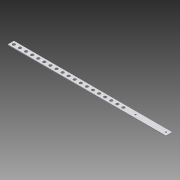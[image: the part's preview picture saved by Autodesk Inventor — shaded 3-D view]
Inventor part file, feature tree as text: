
AUTODESK INVENTOR PART (.ipt)
format: ipt  version: 2015 (Build 190159000, 159)  size: 151,040 bytes
history: native  units: in
note: dims shown in document units (in); Inventor stores cm internally (conversion verified against a paired STEP export)
features: sketch x5, projected_geometry x4, extrude x3, hole x2, pattern_linear x1
ambient origin geometry x8: Origin, YZ Plane, XZ Plane, XY Plane, X Axis, Y Axis, Z Axis, Center Point
bodies: Solid1 (feature_tree)
feature tree (15):
  extrude  "Extrusion1"  Depth=1.0in
  extrude  "Extrusion2"  Depth=0.125in
  hole  "Hole1"  [1 undecoded]
  extrude  "Extrusion3"  Depth=1.0in TaperAngle=0.0deg
  hole  "Hole2"  [1 undecoded]
  pattern_linear  "Rectangular Pattern1"  Spacing1=5.5in  [1 undecoded]
  sketch  "Sketch1"  dims[d0=0.125in d1=1.0in]
  sketch  "Sketch2"  dims[d2=1.0in d3=0.125in]
  projected_geometry  "Projected Loop1"
  sketch  "Sketch3"  dims[d4=26.0in d5=0.0in d6=7.0in]
  projected_geometry  "Projected Loop2"
  sketch  "Sketch4"  dims[d7=0.875in d8=1.0in d9=0.0in]
  projected_geometry  "Projected Loop3"
  sketch  "Sketch5"  dims[d10=0.5in d11=0.5in d12=5.5in d13=0.5in d14=0.2656in d15=0.75in d16=0.375in d17=0.25in d18=0.5635in d19=1.0in d20=0.8108in d21=19.0in d22=0.5in d23=1.0in d24=0.0in d25=0.5in d26=0.5in d27=0.5in d28=0.75in d29=0.375in d30=0.25in d31=0.5635in d32=1.0in d33=0.8108in d34=7.4803in d36=1.0in]
  projected_geometry  "Projected Loop4"
note: 3 required parameter values undecoded (feature->parameter linkage not recoverable at this tier; creation-order binding heuristic only, values carry confidence <= 0.55)
